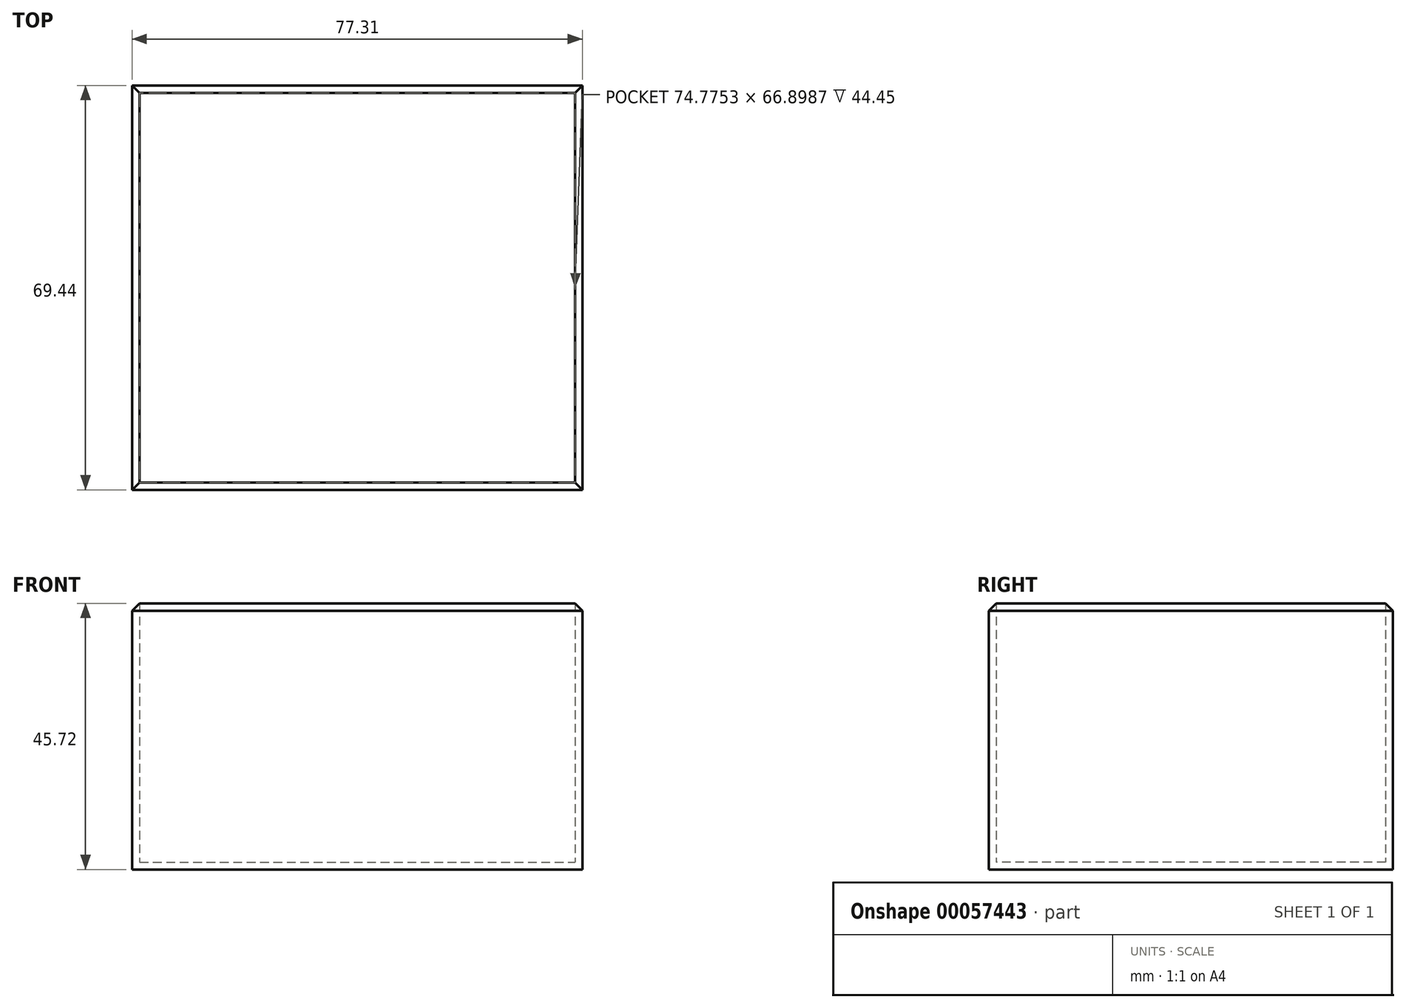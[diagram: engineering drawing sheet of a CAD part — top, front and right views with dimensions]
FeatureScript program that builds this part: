
annotation { "Feature Type Name" : "Feature", "Feature Type Description" : "" }
export const myFeature = defineFeature(function(context is Context, id is Id, definition is map)
    precondition{}
    {
        {
            var Q0;
            Q0=qCreatedBy(makeId("Top.planeOp"),FACE);
            var sketch = newSketch(context, id + "F0", { "sketchPlane" : qUnion([Q0])});
            skLineSegment(sketch, "E0.bottom", {"start": v(-38.76, 29.85) * mm, "end": v(38.55, 29.85) * mm});
            skLineSegment(sketch, "E0.top", {"start": v(-38.76, -39.6) * mm, "end": v(38.55, -39.6) * mm});
            skLineSegment(sketch, "E0.left", {"start": v(-38.76, 29.85) * mm, "end": v(-38.76, -39.6) * mm});
            skLineSegment(sketch, "E0.right", {"start": v(38.55, 29.85) * mm, "end": v(38.55, -39.6) * mm});
            skSolve(sketch);
        }
        {
            var Q0;
            Q0=makeQuery(id+"F0.imprint","IMPRINT",FACE,{"disambiguationData":[TD([[makeQuery(id+"F0.imprint","IMPRINT",EDGE,{"derivedFrom":sQuery(id+"F0.wireOp",EDGE,"E0.bottom")}),-1.0]])]});
            extrude(context, id + "F1", {"entities" : qUnion([Q0]), "depth" : 50.8 * mm});
        }
        {
            var Q0;
            Q0=makeQuery(id+"F1.opExtrude","CAP_FACE",FACE,{"disambiguationData":[OSD([sQuery(id+"F0.wireOp",EDGE,"E0.bottom"),sQuery(id+"F0.wireOp",EDGE,"E0.top"),sQuery(id+"F0.wireOp",EDGE,"E0.left"),sQuery(id+"F0.wireOp",EDGE,"E0.right")])],"isStart":false});
            shell(context, id + "F2", {"entities" : qUnion([Q0]), "thickness" : 1.27 * mm});
        }
        {
            var Q0;
            Q0=makeQuery(id+"F1.opExtrude","CAP_EDGE",EDGE,{"disambiguationData":[OSD([sQuery(id+"F0.wireOp",EDGE,"E0.top")])],"isStart":false});
            var Q1;
            Q1=makeQuery(id+"F1.opExtrude","CAP_EDGE",EDGE,{"disambiguationData":[OSD([sQuery(id+"F0.wireOp",EDGE,"E0.left")])],"isStart":false});
            var Q2;
            Q2=makeQuery(id+"F1.opExtrude","CAP_EDGE",EDGE,{"disambiguationData":[OSD([sQuery(id+"F0.wireOp",EDGE,"E0.bottom")])],"isStart":false});
            var Q3;
            Q3=makeQuery(id+"F1.opExtrude","CAP_EDGE",EDGE,{"disambiguationData":[OSD([sQuery(id+"F0.wireOp",EDGE,"E0.right")])],"isStart":false});
            chamfer(context, id + "F3", {"entities" : qUnion([Q0, Q1, Q2, Q3]), "width" : 6.35 * mm, "tangentPropagation" : true});
        }
        {
            var Q0;
            Q0=qCreatedBy(makeId("Front.planeOp"),FACE);
            var sketch = newSketch(context, id + "F4", { "sketchPlane" : qUnion([Q0])});
            skCircle(sketch, "E1", {"center": v(0, 20.94) * mm, "radius": 9 * mm});
            skSolve(sketch);
        }
        {
            var Q0;
            Q0=sQuery(id+"F4.wireOp",EDGE,"E1");
            extrude(context, id + "F5", {"bodyType" : ToolBodyType.SURFACE, "surfaceEntities" : qUnion([Q0]), "endBound" : BoundingType.SYMMETRIC, "depth" : 127 * mm});
        }
    });
